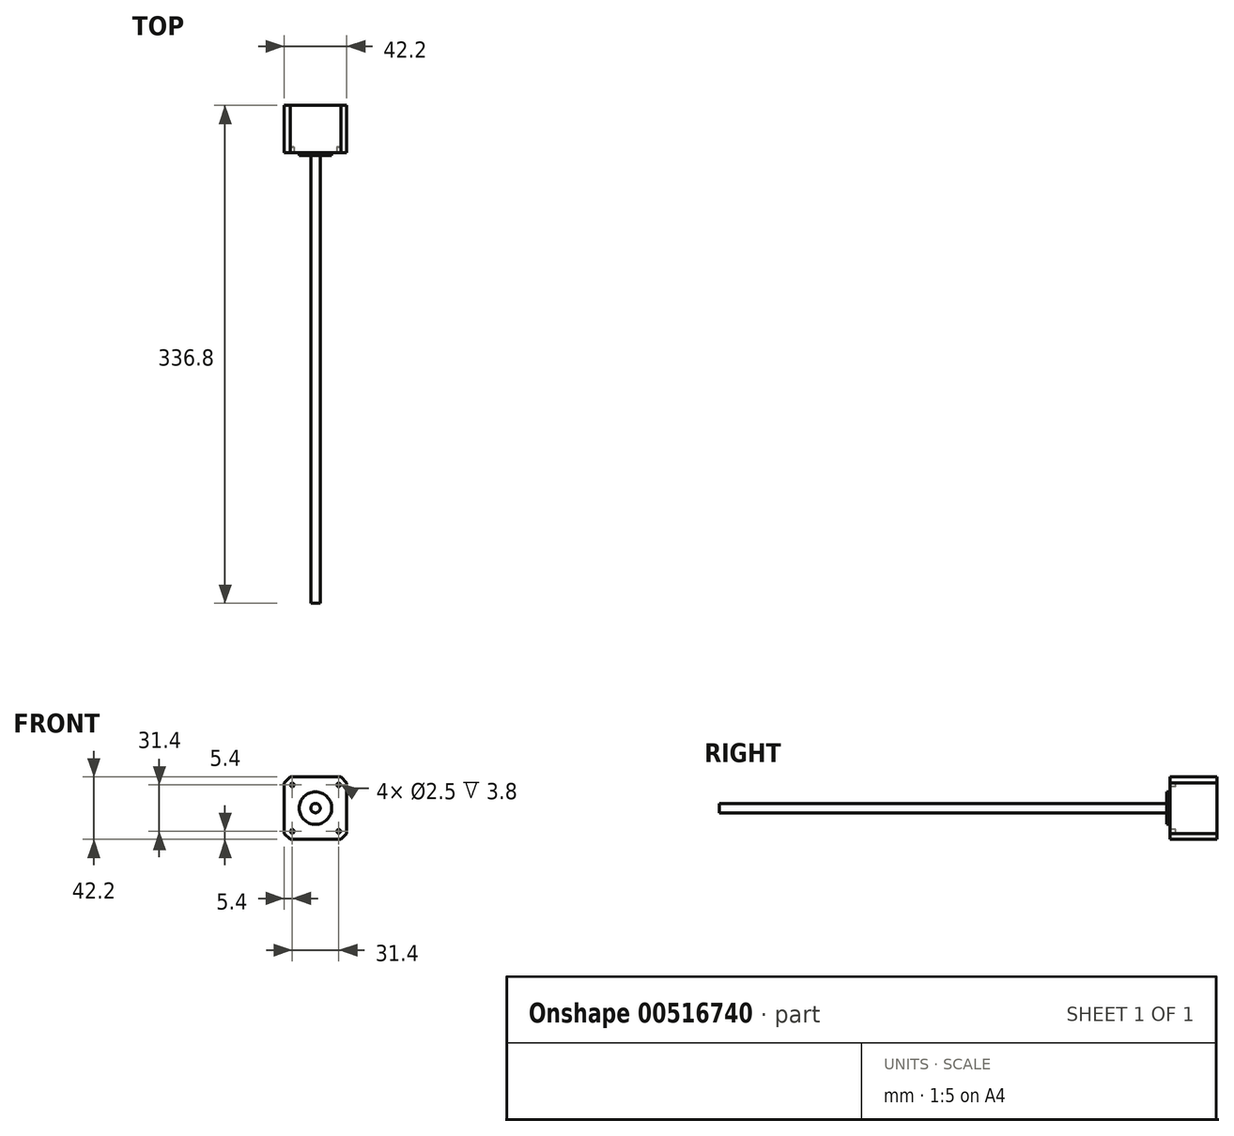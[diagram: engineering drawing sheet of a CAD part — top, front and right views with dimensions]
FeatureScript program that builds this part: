
annotation { "Feature Type Name" : "Feature", "Feature Type Description" : "" }
export const myFeature = defineFeature(function(context is Context, id is Id, definition is map)
    precondition{}
    {
        {
            var Q0;
            Q0=qCreatedBy(makeId("Front.planeOp"),FACE);
            var sketch = newSketch(context, id + "F0", { "sketchPlane" : qUnion([Q0])});
            skLineSegment(sketch, "E0.bottom", {"start": v(21.1, 21.1) * mm, "end": v(-21.1, 21.1) * mm});
            skLineSegment(sketch, "E0.top", {"start": v(21.1, -21.1) * mm, "end": v(-21.1, -21.1) * mm});
            skLineSegment(sketch, "E0.left", {"start": v(21.1, 21.1) * mm, "end": v(21.1, -21.1) * mm});
            skLineSegment(sketch, "E0.right", {"start": v(-21.1, 21.1) * mm, "end": v(-21.1, -21.1) * mm});
            skPoint(sketch, "E0.middle", {"position": v(0, 0) * mm});
            skCircle(sketch, "E1", {"center": v(0, 0) * mm, "radius": 11 * mm});
            skLineSegment(sketch, "E2.bottom", {"start": v(15.7, -15.7) * mm, "end": v(-15.7, -15.7) * mm, "construction": true});
            skLineSegment(sketch, "E2.top", {"start": v(15.7, 15.7) * mm, "end": v(-15.7, 15.7) * mm, "construction": true});
            skLineSegment(sketch, "E2.left", {"start": v(15.7, -15.7) * mm, "end": v(15.7, 15.7) * mm, "construction": true});
            skLineSegment(sketch, "E2.right", {"start": v(-15.7, -15.7) * mm, "end": v(-15.7, 15.7) * mm, "construction": true});
            skCircle(sketch, "E3", {"center": v(-15.7, 15.7) * mm, "radius": 1.25 * mm});
            skCircle(sketch, "E4", {"center": v(15.7, 15.7) * mm, "radius": 1.25 * mm});
            skCircle(sketch, "E5", {"center": v(-15.7, -15.7) * mm, "radius": 1.25 * mm});
            skCircle(sketch, "E6", {"center": v(15.7, -15.7) * mm, "radius": 1.25 * mm});
            skCircle(sketch, "E7", {"center": v(0, 0) * mm, "radius": 3.17 * mm});
            skSolve(sketch);
        }
        {
            var Q0;
            Q0=makeQuery(id+"F0.imprint","IMPRINT",FACE,{"disambiguationData":[TD([[makeQuery(id+"F0.imprint","IMPRINT",EDGE,{"derivedFrom":sQuery(id+"F0.wireOp",EDGE,"E0.bottom")}),1.0]])]});
            var Q1;
            Q1=makeQuery(id+"F0.imprint","IMPRINT",FACE,{"disambiguationData":[TD([[makeQuery(id+"F0.imprint","IMPRINT",EDGE,{"derivedFrom":sQuery(id+"F0.wireOp",EDGE,"E4")}),1.0]])]});
            var Q2;
            Q2=makeQuery(id+"F0.imprint","IMPRINT",FACE,{"disambiguationData":[TD([[makeQuery(id+"F0.imprint","IMPRINT",EDGE,{"derivedFrom":sQuery(id+"F0.wireOp",EDGE,"E6")}),1.0]])]});
            var Q3;
            Q3=makeQuery(id+"F0.imprint","IMPRINT",FACE,{"disambiguationData":[TD([[makeQuery(id+"F0.imprint","IMPRINT",EDGE,{"derivedFrom":sQuery(id+"F0.wireOp",EDGE,"E5")}),1.0]])]});
            var Q4;
            Q4=makeQuery(id+"F0.imprint","IMPRINT",FACE,{"disambiguationData":[TD([[makeQuery(id+"F0.imprint","IMPRINT",EDGE,{"derivedFrom":sQuery(id+"F0.wireOp",EDGE,"E3")}),1.0]])]});
            var Q5;
            Q5=makeQuery(id+"F0.imprint","IMPRINT",FACE,{"disambiguationData":[TD([[makeQuery(id+"F0.imprint","IMPRINT",EDGE,{"derivedFrom":sQuery(id+"F0.wireOp",EDGE,"E1")}),1.0]])]});
            var Q6;
            Q6=makeQuery(id+"F0.imprint","IMPRINT",FACE,{"disambiguationData":[TD([[makeQuery(id+"F0.imprint","IMPRINT",EDGE,{"derivedFrom":sQuery(id+"F0.wireOp",EDGE,"E7")}),1.0]])]});
            extrude(context, id + "F1", {"entities" : qUnion([Q0, Q1, Q2, Q3, Q4, Q5, Q6]), "oppositeDirection" : true, "depth" : 32 * mm, "offsetDistance" : 25 * mm});
        }
        {
            var Q0;
            Q0=makeQuery(id+"F0.imprint","IMPRINT",FACE,{"disambiguationData":[TD([[makeQuery(id+"F0.imprint","IMPRINT",EDGE,{"derivedFrom":sQuery(id+"F0.wireOp",EDGE,"E7")}),1.0]])]});
            extrude(context, id + "F2", {"entities" : qUnion([Q0]), "depth" : 304.8 * mm, "offsetDistance" : 25 * mm});
        }
        {
            var Q0;
            Q0=makeQuery(id+"F0.imprint","IMPRINT",FACE,{"disambiguationData":[TD([[makeQuery(id+"F0.imprint","IMPRINT",EDGE,{"derivedFrom":sQuery(id+"F0.wireOp",EDGE,"E1")}),1.0]])]});
            extrude(context, id + "F3", {"entities" : qUnion([Q0]), "operationType" : NewBodyOperationType.ADD, "depth" : 2 * mm, "offsetDistance" : 25 * mm});
        }
        {
            var Q0;
            Q0=makeQuery(id+"F0.imprint","IMPRINT",FACE,{"disambiguationData":[TD([[makeQuery(id+"F0.imprint","IMPRINT",EDGE,{"derivedFrom":sQuery(id+"F0.wireOp",EDGE,"E3")}),1.0]])]});
            var Q1;
            Q1=makeQuery(id+"F0.imprint","IMPRINT",FACE,{"disambiguationData":[TD([[makeQuery(id+"F0.imprint","IMPRINT",EDGE,{"derivedFrom":sQuery(id+"F0.wireOp",EDGE,"E4")}),1.0]])]});
            var Q2;
            Q2=makeQuery(id+"F0.imprint","IMPRINT",FACE,{"disambiguationData":[TD([[makeQuery(id+"F0.imprint","IMPRINT",EDGE,{"derivedFrom":sQuery(id+"F0.wireOp",EDGE,"E6")}),1.0]])]});
            var Q3;
            Q3=makeQuery(id+"F0.imprint","IMPRINT",FACE,{"disambiguationData":[TD([[makeQuery(id+"F0.imprint","IMPRINT",EDGE,{"derivedFrom":sQuery(id+"F0.wireOp",EDGE,"E5")}),1.0]])]});
            extrude(context, id + "F4", {"entities" : qUnion([Q0, Q1, Q2, Q3]), "operationType" : NewBodyOperationType.REMOVE, "oppositeDirection" : true, "depth" : 3.8 * mm, "offsetDistance" : 25 * mm});
        }
        {
            var Q0;
            Q0=makeQuery(id+"F1.opExtrude","SWEPT_EDGE",EDGE,{"disambiguationData":[OSD([sQuery(id+"F0.wireOp",EDGE,"E0.bottom"),sQuery(id+"F0.wireOp",EDGE,"E0.right")])]});
            var Q1;
            Q1=makeQuery(id+"F1.opExtrude","SWEPT_EDGE",EDGE,{"disambiguationData":[OSD([sQuery(id+"F0.wireOp",EDGE,"E0.bottom"),sQuery(id+"F0.wireOp",EDGE,"E0.left")])]});
            var Q2;
            Q2=makeQuery(id+"F1.opExtrude","SWEPT_EDGE",EDGE,{"disambiguationData":[OSD([sQuery(id+"F0.wireOp",EDGE,"E0.top"),sQuery(id+"F0.wireOp",EDGE,"E0.left")])]});
            var Q3;
            Q3=makeQuery(id+"F1.opExtrude","SWEPT_EDGE",EDGE,{"disambiguationData":[OSD([sQuery(id+"F0.wireOp",EDGE,"E0.top"),sQuery(id+"F0.wireOp",EDGE,"E0.right")])]});
            chamfer(context, id + "F5", {"entities" : qUnion([Q0, Q1, Q2, Q3]), "width" : 4 * mm, "tangentPropagation" : true});
        }
    });
